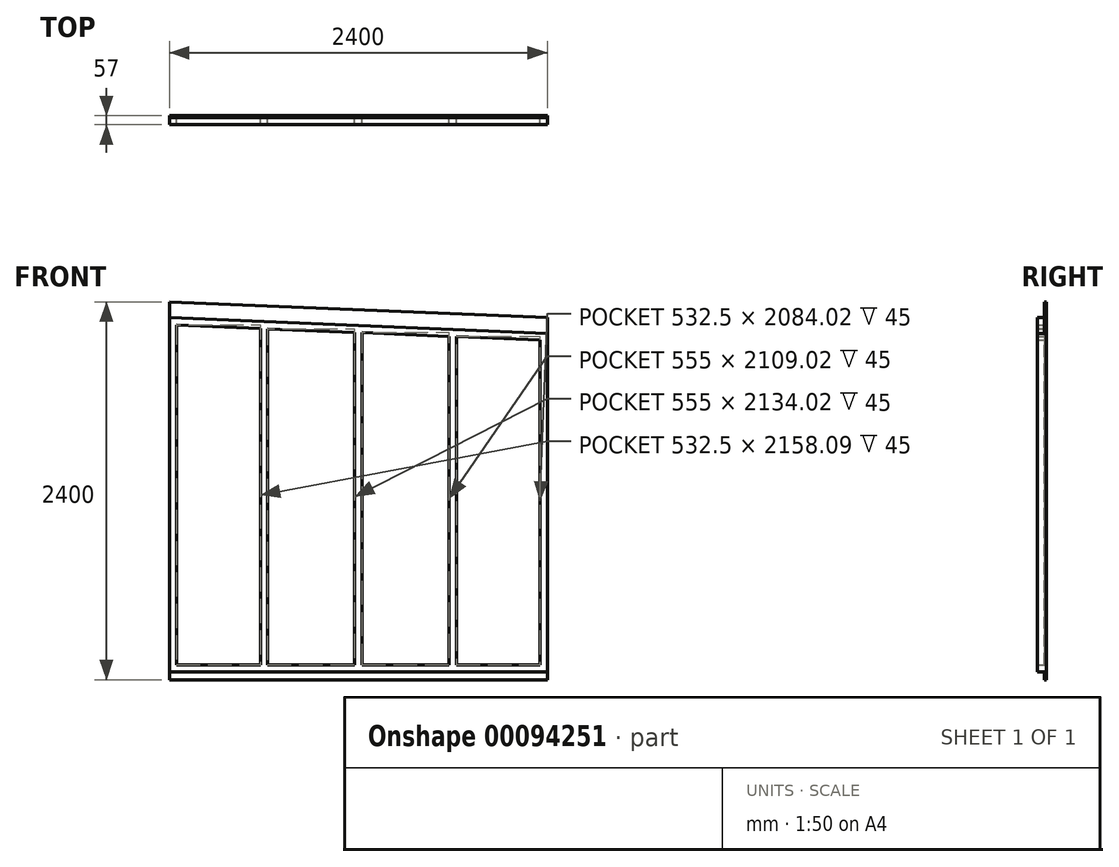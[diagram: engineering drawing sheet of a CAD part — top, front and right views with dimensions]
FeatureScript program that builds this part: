
annotation { "Feature Type Name" : "Feature", "Feature Type Description" : "" }
export const myFeature = defineFeature(function(context is Context, id is Id, definition is map)
    precondition{}
    {
        {
            var Q0;
            Q0=qCreatedBy(makeId("Front.planeOp"),FACE);
            var sketch = newSketch(context, id + "F0", { "sketchPlane" : qUnion([Q0])});
            skLineSegment(sketch, "E0.bottom", {"start": v(1200, -1175) * mm, "end": v(-1200, -1175) * mm});
            skLineSegment(sketch, "E0.left", {"start": v(1200, -1175) * mm, "end": v(1200, 1125) * mm});
            skLineSegment(sketch, "E0.right", {"start": v(-1200, -1175) * mm, "end": v(-1200, 1225) * mm});
            skLineSegment(sketch, "E1", {"start": v(-1200, 1225) * mm, "end": v(1200, 1125) * mm});
            skLineSegment(sketch, "E2", {"start": v(-1200, 1125) * mm, "end": v(1200, 1025) * mm});
            skLineSegment(sketch, "E3", {"start": v(-1200, 1079.96) * mm, "end": v(1200, 979.96) * mm});
            skLineSegment(sketch, "E4", {"start": v(-1200, -1125) * mm, "end": v(1200, -1125) * mm});
            skLineSegment(sketch, "E5", {"start": v(1200, -1080) * mm, "end": v(-1200, -1080) * mm});
            skLineSegment(sketch, "E6", {"start": v(1155, -1080) * mm, "end": v(1155, 981.84) * mm});
            skLineSegment(sketch, "E7", {"start": v(-1155, 1078.09) * mm, "end": v(-1155, -1080) * mm});
            skLineSegment(sketch, "E8", {"start": v(-600, -1080) * mm, "end": v(-600, 1258.53) * mm, "construction": true});
            skLineSegment(sketch, "E9", {"start": v(0, 1332.7) * mm, "end": v(0, -1314.56) * mm, "construction": true});
            skLineSegment(sketch, "E10", {"start": v(600, 1290.83) * mm, "end": v(600, -1080) * mm, "construction": true});
            skLineSegment(sketch, "E11", {"start": v(-622.5, 1055.9) * mm, "end": v(-622.5, -1080) * mm});
            skLineSegment(sketch, "E12", {"start": v(-22.5, 1030.9) * mm, "end": v(-22.5, -1080) * mm});
            skLineSegment(sketch, "E13.MirrorCS", {"start": v(622.5, 1004.02) * mm, "end": v(622.5, -1080) * mm});
            skLineSegment(sketch, "E14.trimOffspring", {"start": v(-577.5, 1054.02) * mm, "end": v(-577.5, -1080) * mm});
            skPoint(sketch, "E15.MirrorCS.start.orphan", {"position": v(-577.5, 1258.61) * mm});
            skPoint(sketch, "E16.orphan", {"position": v(-622.5, 1258.61) * mm});
            skLineSegment(sketch, "E17.trimOffspring", {"start": v(22.5, 1029.02) * mm, "end": v(22.5, -1080) * mm});
            skPoint(sketch, "E18.MirrorCS.start.orphan", {"position": v(22.5, 1253.07) * mm});
            skPoint(sketch, "E19.orphan", {"position": v(-22.5, 1253.07) * mm});
            skLineSegment(sketch, "E20.trimOffspring", {"start": v(577.5, 1005.9) * mm, "end": v(577.5, -1080) * mm});
            skPoint(sketch, "E21.MirrorCS.start.orphan", {"position": v(577.5, 1258.61) * mm});
            skPoint(sketch, "E22.orphan", {"position": v(622.5, 1258.61) * mm});
            skSolve(sketch);
        }
        {
            var Q0;
            {var subQ3=sQuery(id+"F0.wireOp",EDGE,"E2");Q0=makeQuery(id+"F0.imprint","IMPRINT",FACE,{"disambiguationData":[TD([[makeQuery(id+"F0.imprint","IMPRINT",EDGE,{"derivedFrom":subQ3}),-1.0]])]});}
            var Q1;
            {var subQ5=sQuery(id+"F0.wireOp",EDGE,"E7");Q1=makeQuery(id+"F0.imprint","IMPRINT",FACE,{"disambiguationData":[TD([[makeQuery(id+"F0.imprint","IMPRINT",EDGE,{"derivedFrom":subQ5}),-1.0]])]});}
            var Q2;
            {var subQ0=sQuery(id+"F0.wireOp",EDGE,"E11");Q2=makeQuery(id+"F0.imprint","IMPRINT",FACE,{"disambiguationData":[TD([[makeQuery(id+"F0.imprint","IMPRINT",EDGE,{"derivedFrom":subQ0}),1.0]])]});}
            var Q3;
            {var subQ0=sQuery(id+"F0.wireOp",EDGE,"E12");Q3=makeQuery(id+"F0.imprint","IMPRINT",FACE,{"disambiguationData":[TD([[makeQuery(id+"F0.imprint","IMPRINT",EDGE,{"derivedFrom":subQ0}),1.0]])]});}
            var Q4;
            {var subQ0=sQuery(id+"F0.wireOp",EDGE,"E13.MirrorCS");Q4=makeQuery(id+"F0.imprint","IMPRINT",FACE,{"disambiguationData":[TD([[makeQuery(id+"F0.imprint","IMPRINT",EDGE,{"derivedFrom":subQ0}),-1.0]])]});}
            var Q5;
            {var subQ5=sQuery(id+"F0.wireOp",EDGE,"E6");Q5=makeQuery(id+"F0.imprint","IMPRINT",FACE,{"disambiguationData":[TD([[makeQuery(id+"F0.imprint","IMPRINT",EDGE,{"derivedFrom":subQ5}),-1.0]])]});}
            var Q6;
            {var subQ12=sQuery(id+"F0.wireOp",EDGE,"E4");Q6=makeQuery(id+"F0.imprint","IMPRINT",FACE,{"disambiguationData":[TD([[makeQuery(id+"F0.imprint","IMPRINT",EDGE,{"derivedFrom":subQ12}),1.0]])]});}
            extrude(context, id + "F1", {"entities" : qUnion([Q0, Q1, Q2, Q3, Q4, Q5, Q6]), "depth" : 45 * mm});
        }
        {
            var Q0;
            {var subQ0=sQuery(id+"F0.wireOp",EDGE,"E7");Q0=makeQuery(id+"F0.imprint","IMPRINT",FACE,{"disambiguationData":[TD([[makeQuery(id+"F0.imprint","IMPRINT",EDGE,{"derivedFrom":subQ0}),1.0]])]});}
            var Q1;
            {var subQ0=sQuery(id+"F0.wireOp",EDGE,"E12");Q1=makeQuery(id+"F0.imprint","IMPRINT",FACE,{"disambiguationData":[TD([[makeQuery(id+"F0.imprint","IMPRINT",EDGE,{"derivedFrom":subQ0}),-1.0]])]});}
            var Q2;
            {var subQ0=sQuery(id+"F0.wireOp",EDGE,"E17.trimOffspring");Q2=makeQuery(id+"F0.imprint","IMPRINT",FACE,{"disambiguationData":[TD([[makeQuery(id+"F0.imprint","IMPRINT",EDGE,{"derivedFrom":subQ0}),1.0]])]});}
            var Q3;
            {var subQ0=sQuery(id+"F0.wireOp",EDGE,"E6");Q3=makeQuery(id+"F0.imprint","IMPRINT",FACE,{"disambiguationData":[TD([[makeQuery(id+"F0.imprint","IMPRINT",EDGE,{"derivedFrom":subQ0}),1.0]])]});}
            var Q4;
            {var subQ0=sQuery(id+"F0.wireOp",EDGE,"E1");Q4=makeQuery(id+"F0.imprint","IMPRINT",FACE,{"disambiguationData":[TD([[makeQuery(id+"F0.imprint","IMPRINT",EDGE,{"derivedFrom":subQ0}),-1.0]])]});}
            var Q5;
            {var subQ3=sQuery(id+"F0.wireOp",EDGE,"E2");Q5=makeQuery(id+"F0.imprint","IMPRINT",FACE,{"disambiguationData":[TD([[makeQuery(id+"F0.imprint","IMPRINT",EDGE,{"derivedFrom":subQ3}),-1.0]])]});}
            var Q6;
            {var subQ5=sQuery(id+"F0.wireOp",EDGE,"E7");Q6=makeQuery(id+"F0.imprint","IMPRINT",FACE,{"disambiguationData":[TD([[makeQuery(id+"F0.imprint","IMPRINT",EDGE,{"derivedFrom":subQ5}),-1.0]])]});}
            var Q7;
            {var subQ0=sQuery(id+"F0.wireOp",EDGE,"E11");Q7=makeQuery(id+"F0.imprint","IMPRINT",FACE,{"disambiguationData":[TD([[makeQuery(id+"F0.imprint","IMPRINT",EDGE,{"derivedFrom":subQ0}),1.0]])]});}
            var Q8;
            {var subQ0=sQuery(id+"F0.wireOp",EDGE,"E12");Q8=makeQuery(id+"F0.imprint","IMPRINT",FACE,{"disambiguationData":[TD([[makeQuery(id+"F0.imprint","IMPRINT",EDGE,{"derivedFrom":subQ0}),1.0]])]});}
            var Q9;
            {var subQ0=sQuery(id+"F0.wireOp",EDGE,"E13.MirrorCS");Q9=makeQuery(id+"F0.imprint","IMPRINT",FACE,{"disambiguationData":[TD([[makeQuery(id+"F0.imprint","IMPRINT",EDGE,{"derivedFrom":subQ0}),-1.0]])]});}
            var Q10;
            {var subQ5=sQuery(id+"F0.wireOp",EDGE,"E6");Q10=makeQuery(id+"F0.imprint","IMPRINT",FACE,{"disambiguationData":[TD([[makeQuery(id+"F0.imprint","IMPRINT",EDGE,{"derivedFrom":subQ5}),-1.0]])]});}
            var Q11;
            {var subQ12=sQuery(id+"F0.wireOp",EDGE,"E4");Q11=makeQuery(id+"F0.imprint","IMPRINT",FACE,{"disambiguationData":[TD([[makeQuery(id+"F0.imprint","IMPRINT",EDGE,{"derivedFrom":subQ12}),1.0]])]});}
            var Q12;
            {var subQ0=sQuery(id+"F0.wireOp",EDGE,"E0.bottom");Q12=makeQuery(id+"F0.imprint","IMPRINT",FACE,{"disambiguationData":[TD([[makeQuery(id+"F0.imprint","IMPRINT",EDGE,{"derivedFrom":subQ0}),-1.0]])]});}
            extrude(context, id + "F2", {"entities" : qUnion([Q0, Q1, Q2, Q3, Q4, Q5, Q6, Q7, Q8, Q9, Q10, Q11, Q12]), "operationType" : NewBodyOperationType.ADD, "oppositeDirection" : true, "depth" : 12 * mm});
        }
    });
